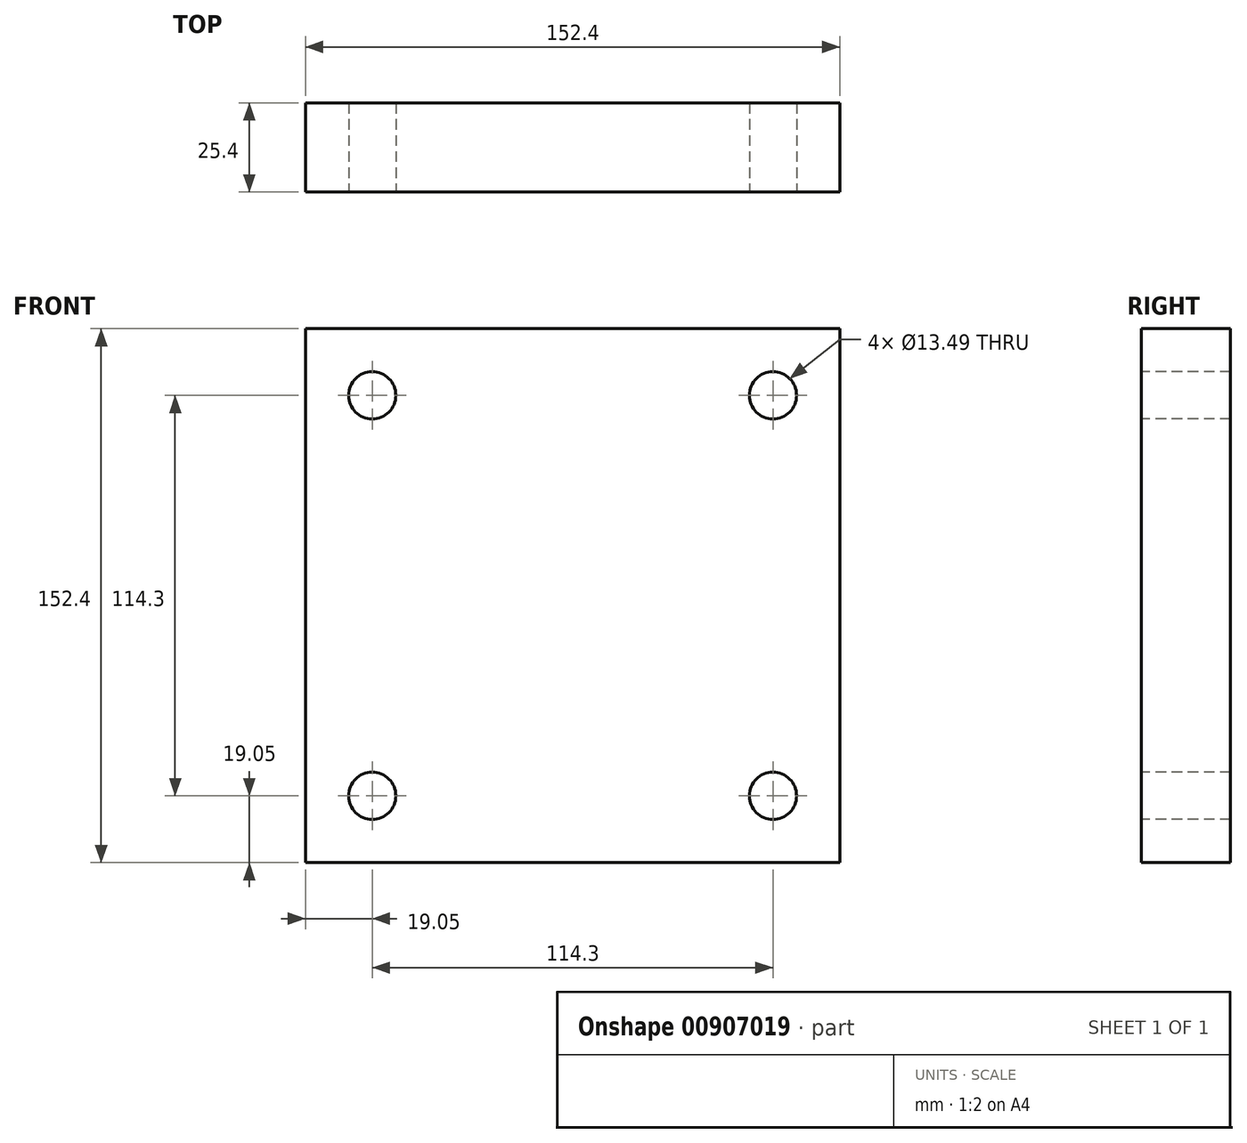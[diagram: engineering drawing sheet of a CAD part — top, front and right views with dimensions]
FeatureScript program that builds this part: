
annotation { "Feature Type Name" : "Feature", "Feature Type Description" : "" }
export const myFeature = defineFeature(function(context is Context, id is Id, definition is map)
    precondition{}
    {
        {
            var Q0;
            Q0=qCreatedBy(makeId("Front.planeOp"),FACE);
            var sketch = newSketch(context, id + "F0", { "sketchPlane" : qUnion([Q0])});
            skLineSegment(sketch, "E0.bottom", {"start": v(76.2, 76.2) * mm, "end": v(-76.2, 76.2) * mm});
            skLineSegment(sketch, "E0.top", {"start": v(76.2, -76.2) * mm, "end": v(-76.2, -76.2) * mm});
            skLineSegment(sketch, "E0.left", {"start": v(76.2, 76.2) * mm, "end": v(76.2, -76.2) * mm});
            skLineSegment(sketch, "E0.right", {"start": v(-76.2, 76.2) * mm, "end": v(-76.2, -76.2) * mm});
            skPoint(sketch, "E0.middle", {"position": v(0, 0) * mm});
            skSolve(sketch);
        }
        {
            var Q0;
            Q0=makeQuery(id+"F0.imprint","IMPRINT",FACE,{"disambiguationData":[TD([[makeQuery(id+"F0.imprint","IMPRINT",EDGE,{"derivedFrom":sQuery(id+"F0.wireOp",EDGE,"E0.bottom")}),1.0]])]});
            extrude(context, id + "F1", {"entities" : qUnion([Q0]), "depth" : 25.4 * mm, "offsetDistance" : 25.4 * mm});
        }
        {
            var Q0;
            Q0=makeQuery(id+"F1.opExtrude","CAP_FACE",FACE,{"disambiguationData":[OSD([sQuery(id+"F0.wireOp",EDGE,"E0.bottom"),sQuery(id+"F0.wireOp",EDGE,"E0.top"),sQuery(id+"F0.wireOp",EDGE,"E0.left"),sQuery(id+"F0.wireOp",EDGE,"E0.right")])],"isStart":false});
            var sketch = newSketch(context, id + "F2", { "sketchPlane" : qUnion([Q0])});
            skLineSegment(sketch, "E1.0", {"start": v(57.15, -57.15) * mm, "end": v(57.15, 57.15) * mm});
            skLineSegment(sketch, "E1.1", {"start": v(-57.15, -57.15) * mm, "end": v(57.15, -57.15) * mm});
            skLineSegment(sketch, "E1.2", {"start": v(-57.15, 57.15) * mm, "end": v(-57.15, -57.15) * mm});
            skLineSegment(sketch, "E1.3", {"start": v(57.15, 57.15) * mm, "end": v(-57.15, 57.15) * mm});
            skSolve(sketch);
        }
        {
            var Q0;
            Q0=sQuery(id+"F2.wireOp",VERTEX,"E1.2.start");
            var Q1;
            Q1=sQuery(id+"F2.wireOp",VERTEX,"E1.0.end");
            var Q2;
            Q2=sQuery(id+"F2.wireOp",VERTEX,"E1.0.start");
            var Q3;
            Q3=sQuery(id+"F2.wireOp",VERTEX,"E1.1.start");
            var Q4;
            Q4=makeQuery(id+"F1.opExtrude","SWEPT_BODY",BODY,{"disambiguationData":[OSD([sQuery(id+"F0.wireOp",EDGE,"E0.bottom"),sQuery(id+"F0.wireOp",EDGE,"E0.top"),sQuery(id+"F0.wireOp",EDGE,"E0.left"),sQuery(id+"F0.wireOp",EDGE,"E0.right")])]});
            hole(context, id + "F3", {"style" : HoleStyle.SIMPLE, "endStyle" : HoleEndStyle.THROUGH, "standardTappedOrClearance" : lookupTablePath({ "fit" : "Free", "standard" : "ANSI", "size" : "1/2", "type" : "Clearance" }), "standardBlindInLast" : lookupTablePath({ "fit" : "Free", "standard" : "ANSI", "engagement" : "75%", "pitch" : "13 tpi", "size" : "1/2", "type" : "Clearance & tapped" }), "holeDiameter" : 13.5 * mm, "majorDiameter" : 12.7 * mm, "isTappedThrough" : true, "tappedDepth" : 12.7 * mm, "tapClearance" : 3, "locations" : qUnion([Q0, Q1, Q2, Q3]), "scope" : qUnion([Q4])});
        }
    });
